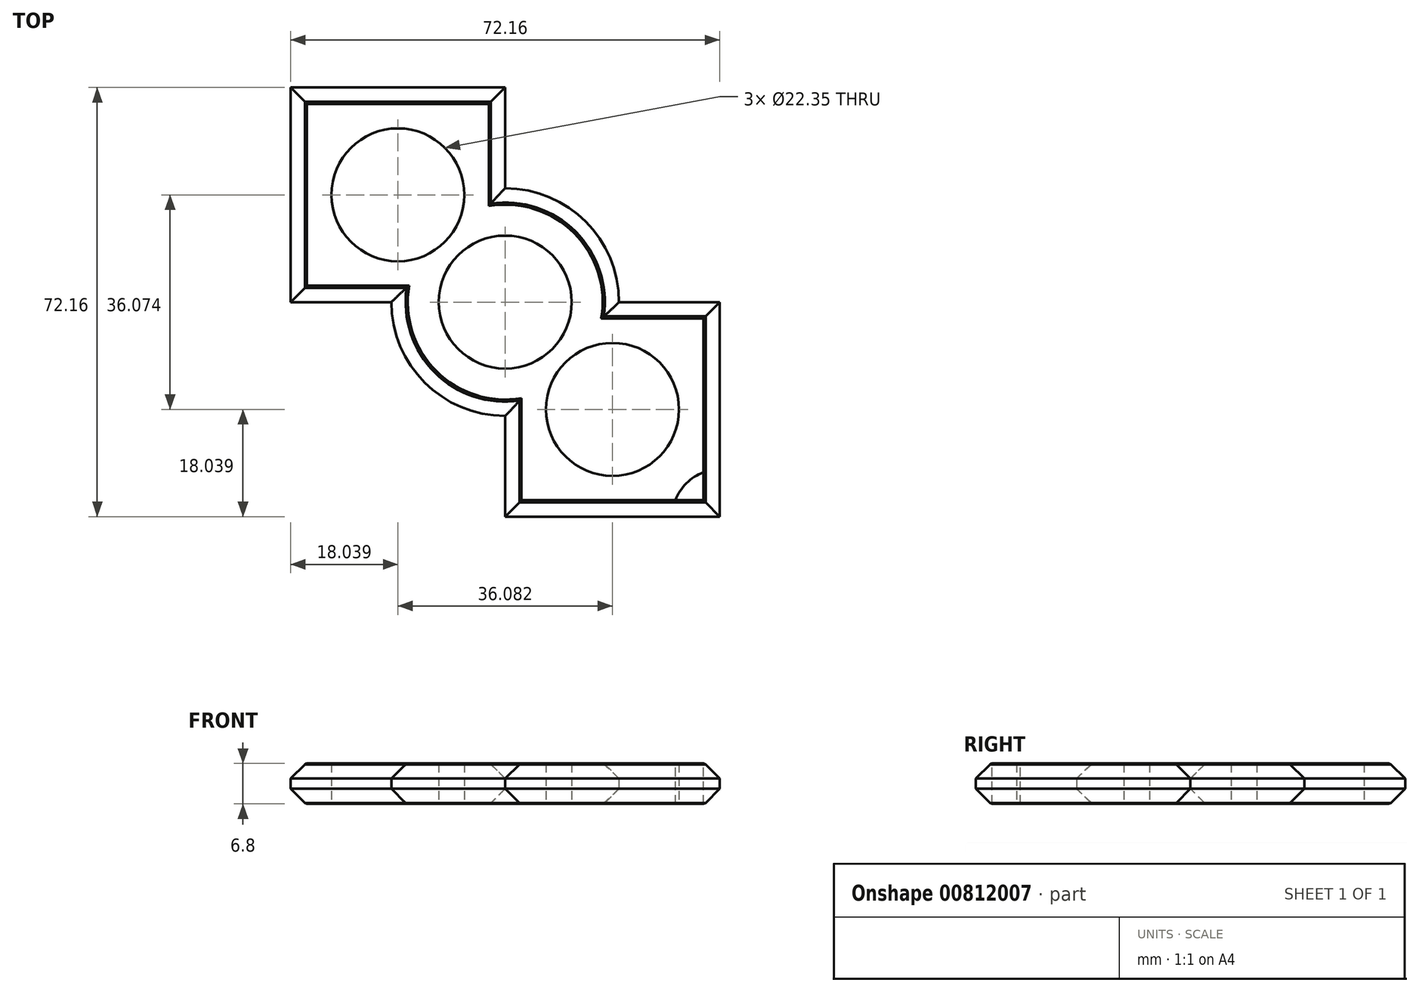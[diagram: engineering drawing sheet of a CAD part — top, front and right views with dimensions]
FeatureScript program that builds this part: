
annotation { "Feature Type Name" : "Feature", "Feature Type Description" : "" }
export const myFeature = defineFeature(function(context is Context, id is Id, definition is map)
    precondition{}
    {
        {
            var Q0;
            Q0=qCreatedBy(makeId("Top.planeOp"),FACE);
            var sketch = newSketch(context, id + "F0", { "sketchPlane" : qUnion([Q0])});
            skLineSegment(sketch, "E0.bottom", {"start": v(0, 0) * mm, "end": v(-36.08, 0) * mm});
            skLineSegment(sketch, "E0.top", {"start": v(0, 36.08) * mm, "end": v(-36.08, 36.08) * mm});
            skLineSegment(sketch, "E0.left", {"start": v(0, 0) * mm, "end": v(0, 36.08) * mm});
            skLineSegment(sketch, "E0.right", {"start": v(-36.08, 0) * mm, "end": v(-36.08, 36.08) * mm});
            skLineSegment(sketch, "E1.bottom", {"start": v(0, 0) * mm, "end": v(36.08, 0) * mm});
            skLineSegment(sketch, "E1.top", {"start": v(0, -36.08) * mm, "end": v(36.08, -36.08) * mm});
            skLineSegment(sketch, "E1.left", {"start": v(0, 0) * mm, "end": v(0, -36.08) * mm});
            skLineSegment(sketch, "E1.right", {"start": v(36.08, 0) * mm, "end": v(36.08, -36.08) * mm});
            skCircle(sketch, "E2", {"center": v(0, 0) * mm, "radius": 19.14 * mm});
            skCircle(sketch, "E3", {"center": v(18.04, -18.04) * mm, "radius": 11.18 * mm});
            skCircle(sketch, "E4", {"center": v(0, 0) * mm, "radius": 11.18 * mm});
            skCircle(sketch, "E5", {"center": v(-18.04, 18.03) * mm, "radius": 11.18 * mm});
            skLineSegment(sketch, "E6", {"start": v(-36.08, 36.08) * mm, "end": v(36.08, -36.08) * mm});
            skLineSegment(sketch, "E7", {"start": v(0, 36.08) * mm, "end": v(-36.08, 0) * mm});
            skLineSegment(sketch, "E8", {"start": v(36.08, 0) * mm, "end": v(0, -36.08) * mm});
            skPoint(sketch, "E9.positionSnap0", {"position": v(-18.04, 18.04) * mm});
            skSolve(sketch);
        }
        {
            var Q0;
            Q0 = qSketchRegion(id + "F0", true);
            extrude(context, id + "F1", {"entities" : qUnion([Q0]), "depth" : 6.8 * mm, "offsetDistance" : 25.4 * mm});
        }
        {
            var Q0;
            {var subQ0=sQuery(id+"F0.wireOp",EDGE,"E2");Q0=makeQuery(id+"F1.opExtrude","CAP_EDGE",EDGE,{"disambiguationData":[OSD([subQ0]),TDD([makeQuery(id+"F0.imprint","IMPRINT",EDGE,{"disambiguationData":[TD([[makeQuery(id+"F0.imprint","INTERSECT",VERTEX,{"derivedFrom":[sQuery(id+"F0.wireOp",EDGE,"E0.bottom"),subQ0]}),-1.0]])],"derivedFrom":subQ0})])],"isStart":false});}
            var Q1;
            {var subQ0=sQuery(id+"F0.wireOp",EDGE,"E2");Q1=makeQuery(id+"F1.opExtrude","CAP_EDGE",EDGE,{"disambiguationData":[OSD([subQ0]),TDD([makeQuery(id+"F0.imprint","IMPRINT",EDGE,{"disambiguationData":[TD([[makeQuery(id+"F0.imprint","INTERSECT",VERTEX,{"derivedFrom":[sQuery(id+"F0.wireOp",EDGE,"E0.bottom"),subQ0]}),-1.0]])],"derivedFrom":subQ0})])],"isStart":true});}
            var Q2;
            Q2=makeQuery(id+"F1.opExtrude","CAP_EDGE",EDGE,{"disambiguationData":[OSD([sQuery(id+"F0.wireOp",EDGE,"E0.bottom")])],"isStart":false});
            var Q3;
            Q3=makeQuery(id+"F1.opExtrude","CAP_EDGE",EDGE,{"disambiguationData":[OSD([sQuery(id+"F0.wireOp",EDGE,"E0.bottom")])],"isStart":true});
            var Q4;
            Q4=makeQuery(id+"F1.opExtrude","CAP_EDGE",EDGE,{"disambiguationData":[OSD([sQuery(id+"F0.wireOp",EDGE,"E1.top")])],"isStart":false});
            var Q5;
            Q5=makeQuery(id+"F1.opExtrude","CAP_EDGE",EDGE,{"disambiguationData":[OSD([sQuery(id+"F0.wireOp",EDGE,"E1.top")])],"isStart":true});
            var Q6;
            Q6=makeQuery(id+"F1.opExtrude","CAP_EDGE",EDGE,{"disambiguationData":[OSD([sQuery(id+"F0.wireOp",EDGE,"E1.left")])],"isStart":true});
            var Q7;
            Q7=makeQuery(id+"F1.opExtrude","CAP_EDGE",EDGE,{"disambiguationData":[OSD([sQuery(id+"F0.wireOp",EDGE,"E1.left")])],"isStart":false});
            var Q8;
            Q8=makeQuery(id+"F1.opExtrude","CAP_EDGE",EDGE,{"disambiguationData":[OSD([sQuery(id+"F0.wireOp",EDGE,"E1.right")])],"isStart":false});
            var Q9;
            Q9=makeQuery(id+"F1.opExtrude","CAP_EDGE",EDGE,{"disambiguationData":[OSD([sQuery(id+"F0.wireOp",EDGE,"E1.right")])],"isStart":true});
            var Q10;
            Q10=makeQuery(id+"F1.opExtrude","CAP_EDGE",EDGE,{"disambiguationData":[OSD([sQuery(id+"F0.wireOp",EDGE,"E1.bottom")])],"isStart":true});
            var Q11;
            Q11=makeQuery(id+"F1.opExtrude","CAP_EDGE",EDGE,{"disambiguationData":[OSD([sQuery(id+"F0.wireOp",EDGE,"E1.bottom")])],"isStart":false});
            var Q12;
            {var subQ0=sQuery(id+"F0.wireOp",EDGE,"E2");Q12=makeQuery(id+"F1.opExtrude","CAP_EDGE",EDGE,{"disambiguationData":[OSD([subQ0]),TDD([makeQuery(id+"F0.imprint","IMPRINT",EDGE,{"disambiguationData":[TD([[makeQuery(id+"F0.imprint","INTERSECT",VERTEX,{"derivedFrom":[sQuery(id+"F0.wireOp",EDGE,"E0.left"),subQ0]}),1.0]])],"derivedFrom":subQ0})])],"isStart":false});}
            var Q13;
            {var subQ0=sQuery(id+"F0.wireOp",EDGE,"E2");Q13=makeQuery(id+"F1.opExtrude","CAP_EDGE",EDGE,{"disambiguationData":[OSD([subQ0]),TDD([makeQuery(id+"F0.imprint","IMPRINT",EDGE,{"disambiguationData":[TD([[makeQuery(id+"F0.imprint","INTERSECT",VERTEX,{"derivedFrom":[sQuery(id+"F0.wireOp",EDGE,"E0.left"),subQ0]}),1.0]])],"derivedFrom":subQ0})])],"isStart":true});}
            var Q14;
            Q14=makeQuery(id+"F1.opExtrude","CAP_EDGE",EDGE,{"disambiguationData":[OSD([sQuery(id+"F0.wireOp",EDGE,"E0.left")])],"isStart":false});
            var Q15;
            Q15=makeQuery(id+"F1.opExtrude","CAP_EDGE",EDGE,{"disambiguationData":[OSD([sQuery(id+"F0.wireOp",EDGE,"E0.left")])],"isStart":true});
            var Q16;
            Q16=makeQuery(id+"F1.opExtrude","CAP_EDGE",EDGE,{"disambiguationData":[OSD([sQuery(id+"F0.wireOp",EDGE,"E0.top")])],"isStart":true});
            var Q17;
            Q17=makeQuery(id+"F1.opExtrude","CAP_EDGE",EDGE,{"disambiguationData":[OSD([sQuery(id+"F0.wireOp",EDGE,"E0.top")])],"isStart":false});
            var Q18;
            Q18=makeQuery(id+"F1.opExtrude","CAP_EDGE",EDGE,{"disambiguationData":[OSD([sQuery(id+"F0.wireOp",EDGE,"E0.right")])],"isStart":false});
            var Q19;
            Q19=makeQuery(id+"F1.opExtrude","CAP_EDGE",EDGE,{"disambiguationData":[OSD([sQuery(id+"F0.wireOp",EDGE,"E0.right")])],"isStart":true});
            chamfer(context, id + "F2", {"entities" : qUnion([Q0, Q1, Q2, Q3, Q4, Q5, Q6, Q7, Q8, Q9, Q10, Q11, Q12, Q13, Q14, Q15, Q16, Q17, Q18, Q19]), "width" : 2.54 * mm, "tangentPropagation" : true});
        }
        {
            var Q0;
            {var subQ0=sQuery(id+"F0.wireOp",EDGE,"E0.right");Q0=makeQuery(id+"F2.opChamfer","BLEND_EDGE",EDGE,{"blendedFrom":[makeQuery(id+"F1.opExtrude","CAP_EDGE",EDGE,{"disambiguationData":[OSD([subQ0])],"isStart":false}),makeQuery(id+"F1.opExtrude","CAP_FACE",FACE,{"disambiguationData":[OSD([sQuery(id+"F0.wireOp",EDGE,"E0.bottom"),sQuery(id+"F0.wireOp",EDGE,"E0.top"),sQuery(id+"F0.wireOp",EDGE,"E0.left"),subQ0,sQuery(id+"F0.wireOp",EDGE,"E1.bottom"),sQuery(id+"F0.wireOp",EDGE,"E1.top"),sQuery(id+"F0.wireOp",EDGE,"E1.left"),sQuery(id+"F0.wireOp",EDGE,"E1.right"),sQuery(id+"F0.wireOp",EDGE,"E2"),sQuery(id+"F0.wireOp",EDGE,"VLRDwp0t-7qAt-eu2T-jZEU-YPBGhESBlTfT"),sQuery(id+"F0.wireOp",EDGE,"WEYKgsFz-RtNv-legM-eSOE-KK9nOp16vvV1"),sQuery(id+"F0.wireOp",EDGE,"XJheyNme-LiQL-8ZLm-PUsm-MQK8YgGBS3Id")])],"isStart":false})],"blendedInto":[makeQuery(id+"F1.opExtrude","CAP_FACE",FACE,{"disambiguationData":[OSD([sQuery(id+"F0.wireOp",EDGE,"E0.bottom"),sQuery(id+"F0.wireOp",EDGE,"E0.top"),sQuery(id+"F0.wireOp",EDGE,"E0.left"),subQ0,sQuery(id+"F0.wireOp",EDGE,"E1.bottom"),sQuery(id+"F0.wireOp",EDGE,"E1.top"),sQuery(id+"F0.wireOp",EDGE,"E1.left"),sQuery(id+"F0.wireOp",EDGE,"E1.right"),sQuery(id+"F0.wireOp",EDGE,"E2"),sQuery(id+"F0.wireOp",EDGE,"VLRDwp0t-7qAt-eu2T-jZEU-YPBGhESBlTfT"),sQuery(id+"F0.wireOp",EDGE,"WEYKgsFz-RtNv-legM-eSOE-KK9nOp16vvV1"),sQuery(id+"F0.wireOp",EDGE,"XJheyNme-LiQL-8ZLm-PUsm-MQK8YgGBS3Id")])],"isStart":false})]});}
            var Q1;
            {var subQ0=sQuery(id+"F0.wireOp",EDGE,"E0.bottom");Q1=makeQuery(id+"F2.opChamfer","BLEND_EDGE",EDGE,{"blendedFrom":[makeQuery(id+"F1.opExtrude","CAP_EDGE",EDGE,{"disambiguationData":[OSD([subQ0])],"isStart":false}),makeQuery(id+"F1.opExtrude","CAP_FACE",FACE,{"disambiguationData":[OSD([subQ0,sQuery(id+"F0.wireOp",EDGE,"E0.top"),sQuery(id+"F0.wireOp",EDGE,"E0.left"),sQuery(id+"F0.wireOp",EDGE,"E0.right"),sQuery(id+"F0.wireOp",EDGE,"E1.bottom"),sQuery(id+"F0.wireOp",EDGE,"E1.top"),sQuery(id+"F0.wireOp",EDGE,"E1.left"),sQuery(id+"F0.wireOp",EDGE,"E1.right"),sQuery(id+"F0.wireOp",EDGE,"E2"),sQuery(id+"F0.wireOp",EDGE,"VLRDwp0t-7qAt-eu2T-jZEU-YPBGhESBlTfT"),sQuery(id+"F0.wireOp",EDGE,"WEYKgsFz-RtNv-legM-eSOE-KK9nOp16vvV1"),sQuery(id+"F0.wireOp",EDGE,"XJheyNme-LiQL-8ZLm-PUsm-MQK8YgGBS3Id")])],"isStart":false})],"blendedInto":[makeQuery(id+"F1.opExtrude","CAP_FACE",FACE,{"disambiguationData":[OSD([subQ0,sQuery(id+"F0.wireOp",EDGE,"E0.top"),sQuery(id+"F0.wireOp",EDGE,"E0.left"),sQuery(id+"F0.wireOp",EDGE,"E0.right"),sQuery(id+"F0.wireOp",EDGE,"E1.bottom"),sQuery(id+"F0.wireOp",EDGE,"E1.top"),sQuery(id+"F0.wireOp",EDGE,"E1.left"),sQuery(id+"F0.wireOp",EDGE,"E1.right"),sQuery(id+"F0.wireOp",EDGE,"E2"),sQuery(id+"F0.wireOp",EDGE,"VLRDwp0t-7qAt-eu2T-jZEU-YPBGhESBlTfT"),sQuery(id+"F0.wireOp",EDGE,"WEYKgsFz-RtNv-legM-eSOE-KK9nOp16vvV1"),sQuery(id+"F0.wireOp",EDGE,"XJheyNme-LiQL-8ZLm-PUsm-MQK8YgGBS3Id")])],"isStart":false})]});}
            var Q2;
            {var subQ0=sQuery(id+"F0.wireOp",EDGE,"E2");var subQ1=sQuery(id+"F0.wireOp",EDGE,"E1.left");var subQ2=sQuery(id+"F0.wireOp",EDGE,"E0.bottom");Q2=makeQuery(id+"F2.opChamfer","BLEND_EDGE",EDGE,{"blendedFrom":[makeQuery(id+"F1.opExtrude","CAP_EDGE",EDGE,{"disambiguationData":[OSD([subQ0]),TDD([makeQuery(id+"F0.imprint","IMPRINT",EDGE,{"disambiguationData":[TD([[makeQuery(id+"F0.imprint","INTERSECT",VERTEX,{"derivedFrom":[subQ2,subQ0]}),-1.0]])],"derivedFrom":subQ0})])],"isStart":false}),makeQuery(id+"F1.opExtrude","CAP_FACE",FACE,{"disambiguationData":[OSD([subQ2,sQuery(id+"F0.wireOp",EDGE,"E0.top"),sQuery(id+"F0.wireOp",EDGE,"E0.left"),sQuery(id+"F0.wireOp",EDGE,"E0.right"),sQuery(id+"F0.wireOp",EDGE,"E1.bottom"),sQuery(id+"F0.wireOp",EDGE,"E1.top"),subQ1,sQuery(id+"F0.wireOp",EDGE,"E1.right"),subQ0,sQuery(id+"F0.wireOp",EDGE,"VLRDwp0t-7qAt-eu2T-jZEU-YPBGhESBlTfT"),sQuery(id+"F0.wireOp",EDGE,"WEYKgsFz-RtNv-legM-eSOE-KK9nOp16vvV1"),sQuery(id+"F0.wireOp",EDGE,"XJheyNme-LiQL-8ZLm-PUsm-MQK8YgGBS3Id")])],"isStart":false})],"blendedInto":[makeQuery(id+"F1.opExtrude","CAP_FACE",FACE,{"disambiguationData":[OSD([subQ2,sQuery(id+"F0.wireOp",EDGE,"E0.top"),sQuery(id+"F0.wireOp",EDGE,"E0.left"),sQuery(id+"F0.wireOp",EDGE,"E0.right"),sQuery(id+"F0.wireOp",EDGE,"E1.bottom"),sQuery(id+"F0.wireOp",EDGE,"E1.top"),subQ1,sQuery(id+"F0.wireOp",EDGE,"E1.right"),subQ0,sQuery(id+"F0.wireOp",EDGE,"VLRDwp0t-7qAt-eu2T-jZEU-YPBGhESBlTfT"),sQuery(id+"F0.wireOp",EDGE,"WEYKgsFz-RtNv-legM-eSOE-KK9nOp16vvV1"),sQuery(id+"F0.wireOp",EDGE,"XJheyNme-LiQL-8ZLm-PUsm-MQK8YgGBS3Id")])],"isStart":false})]});}
            var Q3;
            {var subQ0=sQuery(id+"F0.wireOp",EDGE,"E1.left");Q3=makeQuery(id+"F2.opChamfer","BLEND_EDGE",EDGE,{"blendedFrom":[makeQuery(id+"F1.opExtrude","CAP_EDGE",EDGE,{"disambiguationData":[OSD([subQ0])],"isStart":false}),makeQuery(id+"F1.opExtrude","CAP_FACE",FACE,{"disambiguationData":[OSD([sQuery(id+"F0.wireOp",EDGE,"E0.bottom"),sQuery(id+"F0.wireOp",EDGE,"E0.top"),sQuery(id+"F0.wireOp",EDGE,"E0.left"),sQuery(id+"F0.wireOp",EDGE,"E0.right"),sQuery(id+"F0.wireOp",EDGE,"E1.bottom"),sQuery(id+"F0.wireOp",EDGE,"E1.top"),subQ0,sQuery(id+"F0.wireOp",EDGE,"E1.right"),sQuery(id+"F0.wireOp",EDGE,"E2"),sQuery(id+"F0.wireOp",EDGE,"VLRDwp0t-7qAt-eu2T-jZEU-YPBGhESBlTfT"),sQuery(id+"F0.wireOp",EDGE,"WEYKgsFz-RtNv-legM-eSOE-KK9nOp16vvV1"),sQuery(id+"F0.wireOp",EDGE,"XJheyNme-LiQL-8ZLm-PUsm-MQK8YgGBS3Id")])],"isStart":false})],"blendedInto":[makeQuery(id+"F1.opExtrude","CAP_FACE",FACE,{"disambiguationData":[OSD([sQuery(id+"F0.wireOp",EDGE,"E0.bottom"),sQuery(id+"F0.wireOp",EDGE,"E0.top"),sQuery(id+"F0.wireOp",EDGE,"E0.left"),sQuery(id+"F0.wireOp",EDGE,"E0.right"),sQuery(id+"F0.wireOp",EDGE,"E1.bottom"),sQuery(id+"F0.wireOp",EDGE,"E1.top"),subQ0,sQuery(id+"F0.wireOp",EDGE,"E1.right"),sQuery(id+"F0.wireOp",EDGE,"E2"),sQuery(id+"F0.wireOp",EDGE,"VLRDwp0t-7qAt-eu2T-jZEU-YPBGhESBlTfT"),sQuery(id+"F0.wireOp",EDGE,"WEYKgsFz-RtNv-legM-eSOE-KK9nOp16vvV1"),sQuery(id+"F0.wireOp",EDGE,"XJheyNme-LiQL-8ZLm-PUsm-MQK8YgGBS3Id")])],"isStart":false})]});}
            var Q4;
            {var subQ0=sQuery(id+"F0.wireOp",EDGE,"E1.top");Q4=makeQuery(id+"F2.opChamfer","BLEND_EDGE",EDGE,{"blendedFrom":[makeQuery(id+"F1.opExtrude","CAP_EDGE",EDGE,{"disambiguationData":[OSD([subQ0])],"isStart":false}),makeQuery(id+"F1.opExtrude","CAP_FACE",FACE,{"disambiguationData":[OSD([sQuery(id+"F0.wireOp",EDGE,"E0.bottom"),sQuery(id+"F0.wireOp",EDGE,"E0.top"),sQuery(id+"F0.wireOp",EDGE,"E0.left"),sQuery(id+"F0.wireOp",EDGE,"E0.right"),sQuery(id+"F0.wireOp",EDGE,"E1.bottom"),subQ0,sQuery(id+"F0.wireOp",EDGE,"E1.left"),sQuery(id+"F0.wireOp",EDGE,"E1.right"),sQuery(id+"F0.wireOp",EDGE,"E2"),sQuery(id+"F0.wireOp",EDGE,"VLRDwp0t-7qAt-eu2T-jZEU-YPBGhESBlTfT"),sQuery(id+"F0.wireOp",EDGE,"WEYKgsFz-RtNv-legM-eSOE-KK9nOp16vvV1"),sQuery(id+"F0.wireOp",EDGE,"XJheyNme-LiQL-8ZLm-PUsm-MQK8YgGBS3Id")])],"isStart":false})],"blendedInto":[makeQuery(id+"F1.opExtrude","CAP_FACE",FACE,{"disambiguationData":[OSD([sQuery(id+"F0.wireOp",EDGE,"E0.bottom"),sQuery(id+"F0.wireOp",EDGE,"E0.top"),sQuery(id+"F0.wireOp",EDGE,"E0.left"),sQuery(id+"F0.wireOp",EDGE,"E0.right"),sQuery(id+"F0.wireOp",EDGE,"E1.bottom"),subQ0,sQuery(id+"F0.wireOp",EDGE,"E1.left"),sQuery(id+"F0.wireOp",EDGE,"E1.right"),sQuery(id+"F0.wireOp",EDGE,"E2"),sQuery(id+"F0.wireOp",EDGE,"VLRDwp0t-7qAt-eu2T-jZEU-YPBGhESBlTfT"),sQuery(id+"F0.wireOp",EDGE,"WEYKgsFz-RtNv-legM-eSOE-KK9nOp16vvV1"),sQuery(id+"F0.wireOp",EDGE,"XJheyNme-LiQL-8ZLm-PUsm-MQK8YgGBS3Id")])],"isStart":false})]});}
            var Q5;
            {var subQ0=sQuery(id+"F0.wireOp",EDGE,"E1.right");Q5=makeQuery(id+"F2.opChamfer","BLEND_EDGE",EDGE,{"blendedFrom":[makeQuery(id+"F1.opExtrude","CAP_EDGE",EDGE,{"disambiguationData":[OSD([subQ0])],"isStart":false}),makeQuery(id+"F1.opExtrude","CAP_FACE",FACE,{"disambiguationData":[OSD([sQuery(id+"F0.wireOp",EDGE,"E0.bottom"),sQuery(id+"F0.wireOp",EDGE,"E0.top"),sQuery(id+"F0.wireOp",EDGE,"E0.left"),sQuery(id+"F0.wireOp",EDGE,"E0.right"),sQuery(id+"F0.wireOp",EDGE,"E1.bottom"),sQuery(id+"F0.wireOp",EDGE,"E1.top"),sQuery(id+"F0.wireOp",EDGE,"E1.left"),subQ0,sQuery(id+"F0.wireOp",EDGE,"E2"),sQuery(id+"F0.wireOp",EDGE,"VLRDwp0t-7qAt-eu2T-jZEU-YPBGhESBlTfT"),sQuery(id+"F0.wireOp",EDGE,"WEYKgsFz-RtNv-legM-eSOE-KK9nOp16vvV1"),sQuery(id+"F0.wireOp",EDGE,"XJheyNme-LiQL-8ZLm-PUsm-MQK8YgGBS3Id")])],"isStart":false})],"blendedInto":[makeQuery(id+"F1.opExtrude","CAP_FACE",FACE,{"disambiguationData":[OSD([sQuery(id+"F0.wireOp",EDGE,"E0.bottom"),sQuery(id+"F0.wireOp",EDGE,"E0.top"),sQuery(id+"F0.wireOp",EDGE,"E0.left"),sQuery(id+"F0.wireOp",EDGE,"E0.right"),sQuery(id+"F0.wireOp",EDGE,"E1.bottom"),sQuery(id+"F0.wireOp",EDGE,"E1.top"),sQuery(id+"F0.wireOp",EDGE,"E1.left"),subQ0,sQuery(id+"F0.wireOp",EDGE,"E2"),sQuery(id+"F0.wireOp",EDGE,"VLRDwp0t-7qAt-eu2T-jZEU-YPBGhESBlTfT"),sQuery(id+"F0.wireOp",EDGE,"WEYKgsFz-RtNv-legM-eSOE-KK9nOp16vvV1"),sQuery(id+"F0.wireOp",EDGE,"XJheyNme-LiQL-8ZLm-PUsm-MQK8YgGBS3Id")])],"isStart":false})]});}
            var Q6;
            {var subQ0=sQuery(id+"F0.wireOp",EDGE,"E1.bottom");Q6=makeQuery(id+"F2.opChamfer","BLEND_EDGE",EDGE,{"blendedFrom":[makeQuery(id+"F1.opExtrude","CAP_EDGE",EDGE,{"disambiguationData":[OSD([subQ0])],"isStart":false}),makeQuery(id+"F1.opExtrude","CAP_FACE",FACE,{"disambiguationData":[OSD([sQuery(id+"F0.wireOp",EDGE,"E0.bottom"),sQuery(id+"F0.wireOp",EDGE,"E0.top"),sQuery(id+"F0.wireOp",EDGE,"E0.left"),sQuery(id+"F0.wireOp",EDGE,"E0.right"),subQ0,sQuery(id+"F0.wireOp",EDGE,"E1.top"),sQuery(id+"F0.wireOp",EDGE,"E1.left"),sQuery(id+"F0.wireOp",EDGE,"E1.right"),sQuery(id+"F0.wireOp",EDGE,"E2"),sQuery(id+"F0.wireOp",EDGE,"VLRDwp0t-7qAt-eu2T-jZEU-YPBGhESBlTfT"),sQuery(id+"F0.wireOp",EDGE,"WEYKgsFz-RtNv-legM-eSOE-KK9nOp16vvV1"),sQuery(id+"F0.wireOp",EDGE,"XJheyNme-LiQL-8ZLm-PUsm-MQK8YgGBS3Id")])],"isStart":false})],"blendedInto":[makeQuery(id+"F1.opExtrude","CAP_FACE",FACE,{"disambiguationData":[OSD([sQuery(id+"F0.wireOp",EDGE,"E0.bottom"),sQuery(id+"F0.wireOp",EDGE,"E0.top"),sQuery(id+"F0.wireOp",EDGE,"E0.left"),sQuery(id+"F0.wireOp",EDGE,"E0.right"),subQ0,sQuery(id+"F0.wireOp",EDGE,"E1.top"),sQuery(id+"F0.wireOp",EDGE,"E1.left"),sQuery(id+"F0.wireOp",EDGE,"E1.right"),sQuery(id+"F0.wireOp",EDGE,"E2"),sQuery(id+"F0.wireOp",EDGE,"VLRDwp0t-7qAt-eu2T-jZEU-YPBGhESBlTfT"),sQuery(id+"F0.wireOp",EDGE,"WEYKgsFz-RtNv-legM-eSOE-KK9nOp16vvV1"),sQuery(id+"F0.wireOp",EDGE,"XJheyNme-LiQL-8ZLm-PUsm-MQK8YgGBS3Id")])],"isStart":false})]});}
            var Q7;
            {var subQ0=sQuery(id+"F0.wireOp",EDGE,"E2");var subQ1=sQuery(id+"F0.wireOp",EDGE,"E1.bottom");var subQ2=sQuery(id+"F0.wireOp",EDGE,"E0.left");Q7=makeQuery(id+"F2.opChamfer","BLEND_EDGE",EDGE,{"blendedFrom":[makeQuery(id+"F1.opExtrude","CAP_EDGE",EDGE,{"disambiguationData":[OSD([subQ0]),TDD([makeQuery(id+"F0.imprint","IMPRINT",EDGE,{"disambiguationData":[TD([[makeQuery(id+"F0.imprint","INTERSECT",VERTEX,{"derivedFrom":[subQ2,subQ0]}),1.0]])],"derivedFrom":subQ0})])],"isStart":false}),makeQuery(id+"F1.opExtrude","CAP_FACE",FACE,{"disambiguationData":[OSD([sQuery(id+"F0.wireOp",EDGE,"E0.bottom"),sQuery(id+"F0.wireOp",EDGE,"E0.top"),subQ2,sQuery(id+"F0.wireOp",EDGE,"E0.right"),subQ1,sQuery(id+"F0.wireOp",EDGE,"E1.top"),sQuery(id+"F0.wireOp",EDGE,"E1.left"),sQuery(id+"F0.wireOp",EDGE,"E1.right"),subQ0,sQuery(id+"F0.wireOp",EDGE,"VLRDwp0t-7qAt-eu2T-jZEU-YPBGhESBlTfT"),sQuery(id+"F0.wireOp",EDGE,"WEYKgsFz-RtNv-legM-eSOE-KK9nOp16vvV1"),sQuery(id+"F0.wireOp",EDGE,"XJheyNme-LiQL-8ZLm-PUsm-MQK8YgGBS3Id")])],"isStart":false})],"blendedInto":[makeQuery(id+"F1.opExtrude","CAP_FACE",FACE,{"disambiguationData":[OSD([sQuery(id+"F0.wireOp",EDGE,"E0.bottom"),sQuery(id+"F0.wireOp",EDGE,"E0.top"),subQ2,sQuery(id+"F0.wireOp",EDGE,"E0.right"),subQ1,sQuery(id+"F0.wireOp",EDGE,"E1.top"),sQuery(id+"F0.wireOp",EDGE,"E1.left"),sQuery(id+"F0.wireOp",EDGE,"E1.right"),subQ0,sQuery(id+"F0.wireOp",EDGE,"VLRDwp0t-7qAt-eu2T-jZEU-YPBGhESBlTfT"),sQuery(id+"F0.wireOp",EDGE,"WEYKgsFz-RtNv-legM-eSOE-KK9nOp16vvV1"),sQuery(id+"F0.wireOp",EDGE,"XJheyNme-LiQL-8ZLm-PUsm-MQK8YgGBS3Id")])],"isStart":false})]});}
            var Q8;
            {var subQ0=sQuery(id+"F0.wireOp",EDGE,"E0.left");Q8=makeQuery(id+"F2.opChamfer","BLEND_EDGE",EDGE,{"blendedFrom":[makeQuery(id+"F1.opExtrude","CAP_EDGE",EDGE,{"disambiguationData":[OSD([subQ0])],"isStart":false}),makeQuery(id+"F1.opExtrude","CAP_FACE",FACE,{"disambiguationData":[OSD([sQuery(id+"F0.wireOp",EDGE,"E0.bottom"),sQuery(id+"F0.wireOp",EDGE,"E0.top"),subQ0,sQuery(id+"F0.wireOp",EDGE,"E0.right"),sQuery(id+"F0.wireOp",EDGE,"E1.bottom"),sQuery(id+"F0.wireOp",EDGE,"E1.top"),sQuery(id+"F0.wireOp",EDGE,"E1.left"),sQuery(id+"F0.wireOp",EDGE,"E1.right"),sQuery(id+"F0.wireOp",EDGE,"E2"),sQuery(id+"F0.wireOp",EDGE,"VLRDwp0t-7qAt-eu2T-jZEU-YPBGhESBlTfT"),sQuery(id+"F0.wireOp",EDGE,"WEYKgsFz-RtNv-legM-eSOE-KK9nOp16vvV1"),sQuery(id+"F0.wireOp",EDGE,"XJheyNme-LiQL-8ZLm-PUsm-MQK8YgGBS3Id")])],"isStart":false})],"blendedInto":[makeQuery(id+"F1.opExtrude","CAP_FACE",FACE,{"disambiguationData":[OSD([sQuery(id+"F0.wireOp",EDGE,"E0.bottom"),sQuery(id+"F0.wireOp",EDGE,"E0.top"),subQ0,sQuery(id+"F0.wireOp",EDGE,"E0.right"),sQuery(id+"F0.wireOp",EDGE,"E1.bottom"),sQuery(id+"F0.wireOp",EDGE,"E1.top"),sQuery(id+"F0.wireOp",EDGE,"E1.left"),sQuery(id+"F0.wireOp",EDGE,"E1.right"),sQuery(id+"F0.wireOp",EDGE,"E2"),sQuery(id+"F0.wireOp",EDGE,"VLRDwp0t-7qAt-eu2T-jZEU-YPBGhESBlTfT"),sQuery(id+"F0.wireOp",EDGE,"WEYKgsFz-RtNv-legM-eSOE-KK9nOp16vvV1"),sQuery(id+"F0.wireOp",EDGE,"XJheyNme-LiQL-8ZLm-PUsm-MQK8YgGBS3Id")])],"isStart":false})]});}
            var Q9;
            {var subQ0=sQuery(id+"F0.wireOp",EDGE,"E0.top");Q9=makeQuery(id+"F2.opChamfer","BLEND_EDGE",EDGE,{"blendedFrom":[makeQuery(id+"F1.opExtrude","CAP_EDGE",EDGE,{"disambiguationData":[OSD([subQ0])],"isStart":false}),makeQuery(id+"F1.opExtrude","CAP_FACE",FACE,{"disambiguationData":[OSD([sQuery(id+"F0.wireOp",EDGE,"E0.bottom"),subQ0,sQuery(id+"F0.wireOp",EDGE,"E0.left"),sQuery(id+"F0.wireOp",EDGE,"E0.right"),sQuery(id+"F0.wireOp",EDGE,"E1.bottom"),sQuery(id+"F0.wireOp",EDGE,"E1.top"),sQuery(id+"F0.wireOp",EDGE,"E1.left"),sQuery(id+"F0.wireOp",EDGE,"E1.right"),sQuery(id+"F0.wireOp",EDGE,"E2"),sQuery(id+"F0.wireOp",EDGE,"VLRDwp0t-7qAt-eu2T-jZEU-YPBGhESBlTfT"),sQuery(id+"F0.wireOp",EDGE,"WEYKgsFz-RtNv-legM-eSOE-KK9nOp16vvV1"),sQuery(id+"F0.wireOp",EDGE,"XJheyNme-LiQL-8ZLm-PUsm-MQK8YgGBS3Id")])],"isStart":false})],"blendedInto":[makeQuery(id+"F1.opExtrude","CAP_FACE",FACE,{"disambiguationData":[OSD([sQuery(id+"F0.wireOp",EDGE,"E0.bottom"),subQ0,sQuery(id+"F0.wireOp",EDGE,"E0.left"),sQuery(id+"F0.wireOp",EDGE,"E0.right"),sQuery(id+"F0.wireOp",EDGE,"E1.bottom"),sQuery(id+"F0.wireOp",EDGE,"E1.top"),sQuery(id+"F0.wireOp",EDGE,"E1.left"),sQuery(id+"F0.wireOp",EDGE,"E1.right"),sQuery(id+"F0.wireOp",EDGE,"E2"),sQuery(id+"F0.wireOp",EDGE,"VLRDwp0t-7qAt-eu2T-jZEU-YPBGhESBlTfT"),sQuery(id+"F0.wireOp",EDGE,"WEYKgsFz-RtNv-legM-eSOE-KK9nOp16vvV1"),sQuery(id+"F0.wireOp",EDGE,"XJheyNme-LiQL-8ZLm-PUsm-MQK8YgGBS3Id")])],"isStart":false})]});}
            var Q10;
            {var subQ0=sQuery(id+"F0.wireOp",EDGE,"E1.right");Q10=makeQuery(id+"F2.opChamfer","BLEND_EDGE",EDGE,{"blendedFrom":[makeQuery(id+"F1.opExtrude","CAP_EDGE",EDGE,{"disambiguationData":[OSD([subQ0])],"isStart":true}),makeQuery(id+"F1.opExtrude","CAP_FACE",FACE,{"disambiguationData":[OSD([sQuery(id+"F0.wireOp",EDGE,"E0.bottom"),sQuery(id+"F0.wireOp",EDGE,"E0.top"),sQuery(id+"F0.wireOp",EDGE,"E0.left"),sQuery(id+"F0.wireOp",EDGE,"E0.right"),sQuery(id+"F0.wireOp",EDGE,"E1.bottom"),sQuery(id+"F0.wireOp",EDGE,"E1.top"),sQuery(id+"F0.wireOp",EDGE,"E1.left"),subQ0,sQuery(id+"F0.wireOp",EDGE,"E2"),sQuery(id+"F0.wireOp",EDGE,"VLRDwp0t-7qAt-eu2T-jZEU-YPBGhESBlTfT"),sQuery(id+"F0.wireOp",EDGE,"WEYKgsFz-RtNv-legM-eSOE-KK9nOp16vvV1"),sQuery(id+"F0.wireOp",EDGE,"XJheyNme-LiQL-8ZLm-PUsm-MQK8YgGBS3Id")])],"isStart":true})],"blendedInto":[makeQuery(id+"F1.opExtrude","CAP_FACE",FACE,{"disambiguationData":[OSD([sQuery(id+"F0.wireOp",EDGE,"E0.bottom"),sQuery(id+"F0.wireOp",EDGE,"E0.top"),sQuery(id+"F0.wireOp",EDGE,"E0.left"),sQuery(id+"F0.wireOp",EDGE,"E0.right"),sQuery(id+"F0.wireOp",EDGE,"E1.bottom"),sQuery(id+"F0.wireOp",EDGE,"E1.top"),sQuery(id+"F0.wireOp",EDGE,"E1.left"),subQ0,sQuery(id+"F0.wireOp",EDGE,"E2"),sQuery(id+"F0.wireOp",EDGE,"VLRDwp0t-7qAt-eu2T-jZEU-YPBGhESBlTfT"),sQuery(id+"F0.wireOp",EDGE,"WEYKgsFz-RtNv-legM-eSOE-KK9nOp16vvV1"),sQuery(id+"F0.wireOp",EDGE,"XJheyNme-LiQL-8ZLm-PUsm-MQK8YgGBS3Id")])],"isStart":true})]});}
            var Q11;
            {var subQ0=sQuery(id+"F0.wireOp",EDGE,"E1.top");Q11=makeQuery(id+"F2.opChamfer","BLEND_EDGE",EDGE,{"blendedFrom":[makeQuery(id+"F1.opExtrude","CAP_EDGE",EDGE,{"disambiguationData":[OSD([subQ0])],"isStart":true}),makeQuery(id+"F1.opExtrude","CAP_FACE",FACE,{"disambiguationData":[OSD([sQuery(id+"F0.wireOp",EDGE,"E0.bottom"),sQuery(id+"F0.wireOp",EDGE,"E0.top"),sQuery(id+"F0.wireOp",EDGE,"E0.left"),sQuery(id+"F0.wireOp",EDGE,"E0.right"),sQuery(id+"F0.wireOp",EDGE,"E1.bottom"),subQ0,sQuery(id+"F0.wireOp",EDGE,"E1.left"),sQuery(id+"F0.wireOp",EDGE,"E1.right"),sQuery(id+"F0.wireOp",EDGE,"E2"),sQuery(id+"F0.wireOp",EDGE,"VLRDwp0t-7qAt-eu2T-jZEU-YPBGhESBlTfT"),sQuery(id+"F0.wireOp",EDGE,"WEYKgsFz-RtNv-legM-eSOE-KK9nOp16vvV1"),sQuery(id+"F0.wireOp",EDGE,"XJheyNme-LiQL-8ZLm-PUsm-MQK8YgGBS3Id")])],"isStart":true})],"blendedInto":[makeQuery(id+"F1.opExtrude","CAP_FACE",FACE,{"disambiguationData":[OSD([sQuery(id+"F0.wireOp",EDGE,"E0.bottom"),sQuery(id+"F0.wireOp",EDGE,"E0.top"),sQuery(id+"F0.wireOp",EDGE,"E0.left"),sQuery(id+"F0.wireOp",EDGE,"E0.right"),sQuery(id+"F0.wireOp",EDGE,"E1.bottom"),subQ0,sQuery(id+"F0.wireOp",EDGE,"E1.left"),sQuery(id+"F0.wireOp",EDGE,"E1.right"),sQuery(id+"F0.wireOp",EDGE,"E2"),sQuery(id+"F0.wireOp",EDGE,"VLRDwp0t-7qAt-eu2T-jZEU-YPBGhESBlTfT"),sQuery(id+"F0.wireOp",EDGE,"WEYKgsFz-RtNv-legM-eSOE-KK9nOp16vvV1"),sQuery(id+"F0.wireOp",EDGE,"XJheyNme-LiQL-8ZLm-PUsm-MQK8YgGBS3Id")])],"isStart":true})]});}
            var Q12;
            {var subQ0=sQuery(id+"F0.wireOp",EDGE,"E1.left");Q12=makeQuery(id+"F2.opChamfer","BLEND_EDGE",EDGE,{"blendedFrom":[makeQuery(id+"F1.opExtrude","CAP_EDGE",EDGE,{"disambiguationData":[OSD([subQ0])],"isStart":true}),makeQuery(id+"F1.opExtrude","CAP_FACE",FACE,{"disambiguationData":[OSD([sQuery(id+"F0.wireOp",EDGE,"E0.bottom"),sQuery(id+"F0.wireOp",EDGE,"E0.top"),sQuery(id+"F0.wireOp",EDGE,"E0.left"),sQuery(id+"F0.wireOp",EDGE,"E0.right"),sQuery(id+"F0.wireOp",EDGE,"E1.bottom"),sQuery(id+"F0.wireOp",EDGE,"E1.top"),subQ0,sQuery(id+"F0.wireOp",EDGE,"E1.right"),sQuery(id+"F0.wireOp",EDGE,"E2"),sQuery(id+"F0.wireOp",EDGE,"VLRDwp0t-7qAt-eu2T-jZEU-YPBGhESBlTfT"),sQuery(id+"F0.wireOp",EDGE,"WEYKgsFz-RtNv-legM-eSOE-KK9nOp16vvV1"),sQuery(id+"F0.wireOp",EDGE,"XJheyNme-LiQL-8ZLm-PUsm-MQK8YgGBS3Id")])],"isStart":true})],"blendedInto":[makeQuery(id+"F1.opExtrude","CAP_FACE",FACE,{"disambiguationData":[OSD([sQuery(id+"F0.wireOp",EDGE,"E0.bottom"),sQuery(id+"F0.wireOp",EDGE,"E0.top"),sQuery(id+"F0.wireOp",EDGE,"E0.left"),sQuery(id+"F0.wireOp",EDGE,"E0.right"),sQuery(id+"F0.wireOp",EDGE,"E1.bottom"),sQuery(id+"F0.wireOp",EDGE,"E1.top"),subQ0,sQuery(id+"F0.wireOp",EDGE,"E1.right"),sQuery(id+"F0.wireOp",EDGE,"E2"),sQuery(id+"F0.wireOp",EDGE,"VLRDwp0t-7qAt-eu2T-jZEU-YPBGhESBlTfT"),sQuery(id+"F0.wireOp",EDGE,"WEYKgsFz-RtNv-legM-eSOE-KK9nOp16vvV1"),sQuery(id+"F0.wireOp",EDGE,"XJheyNme-LiQL-8ZLm-PUsm-MQK8YgGBS3Id")])],"isStart":true})]});}
            var Q13;
            {var subQ0=sQuery(id+"F0.wireOp",EDGE,"E2");var subQ1=sQuery(id+"F0.wireOp",EDGE,"E1.left");var subQ2=sQuery(id+"F0.wireOp",EDGE,"E0.bottom");Q13=makeQuery(id+"F2.opChamfer","BLEND_EDGE",EDGE,{"blendedFrom":[makeQuery(id+"F1.opExtrude","CAP_EDGE",EDGE,{"disambiguationData":[OSD([subQ0]),TDD([makeQuery(id+"F0.imprint","IMPRINT",EDGE,{"disambiguationData":[TD([[makeQuery(id+"F0.imprint","INTERSECT",VERTEX,{"derivedFrom":[subQ2,subQ0]}),-1.0]])],"derivedFrom":subQ0})])],"isStart":true}),makeQuery(id+"F1.opExtrude","CAP_FACE",FACE,{"disambiguationData":[OSD([subQ2,sQuery(id+"F0.wireOp",EDGE,"E0.top"),sQuery(id+"F0.wireOp",EDGE,"E0.left"),sQuery(id+"F0.wireOp",EDGE,"E0.right"),sQuery(id+"F0.wireOp",EDGE,"E1.bottom"),sQuery(id+"F0.wireOp",EDGE,"E1.top"),subQ1,sQuery(id+"F0.wireOp",EDGE,"E1.right"),subQ0,sQuery(id+"F0.wireOp",EDGE,"VLRDwp0t-7qAt-eu2T-jZEU-YPBGhESBlTfT"),sQuery(id+"F0.wireOp",EDGE,"WEYKgsFz-RtNv-legM-eSOE-KK9nOp16vvV1"),sQuery(id+"F0.wireOp",EDGE,"XJheyNme-LiQL-8ZLm-PUsm-MQK8YgGBS3Id")])],"isStart":true})],"blendedInto":[makeQuery(id+"F1.opExtrude","CAP_FACE",FACE,{"disambiguationData":[OSD([subQ2,sQuery(id+"F0.wireOp",EDGE,"E0.top"),sQuery(id+"F0.wireOp",EDGE,"E0.left"),sQuery(id+"F0.wireOp",EDGE,"E0.right"),sQuery(id+"F0.wireOp",EDGE,"E1.bottom"),sQuery(id+"F0.wireOp",EDGE,"E1.top"),subQ1,sQuery(id+"F0.wireOp",EDGE,"E1.right"),subQ0,sQuery(id+"F0.wireOp",EDGE,"VLRDwp0t-7qAt-eu2T-jZEU-YPBGhESBlTfT"),sQuery(id+"F0.wireOp",EDGE,"WEYKgsFz-RtNv-legM-eSOE-KK9nOp16vvV1"),sQuery(id+"F0.wireOp",EDGE,"XJheyNme-LiQL-8ZLm-PUsm-MQK8YgGBS3Id")])],"isStart":true})]});}
            var Q14;
            {var subQ0=sQuery(id+"F0.wireOp",EDGE,"E0.bottom");Q14=makeQuery(id+"F2.opChamfer","BLEND_EDGE",EDGE,{"blendedFrom":[makeQuery(id+"F1.opExtrude","CAP_EDGE",EDGE,{"disambiguationData":[OSD([subQ0])],"isStart":true}),makeQuery(id+"F1.opExtrude","CAP_FACE",FACE,{"disambiguationData":[OSD([subQ0,sQuery(id+"F0.wireOp",EDGE,"E0.top"),sQuery(id+"F0.wireOp",EDGE,"E0.left"),sQuery(id+"F0.wireOp",EDGE,"E0.right"),sQuery(id+"F0.wireOp",EDGE,"E1.bottom"),sQuery(id+"F0.wireOp",EDGE,"E1.top"),sQuery(id+"F0.wireOp",EDGE,"E1.left"),sQuery(id+"F0.wireOp",EDGE,"E1.right"),sQuery(id+"F0.wireOp",EDGE,"E2"),sQuery(id+"F0.wireOp",EDGE,"VLRDwp0t-7qAt-eu2T-jZEU-YPBGhESBlTfT"),sQuery(id+"F0.wireOp",EDGE,"WEYKgsFz-RtNv-legM-eSOE-KK9nOp16vvV1"),sQuery(id+"F0.wireOp",EDGE,"XJheyNme-LiQL-8ZLm-PUsm-MQK8YgGBS3Id")])],"isStart":true})],"blendedInto":[makeQuery(id+"F1.opExtrude","CAP_FACE",FACE,{"disambiguationData":[OSD([subQ0,sQuery(id+"F0.wireOp",EDGE,"E0.top"),sQuery(id+"F0.wireOp",EDGE,"E0.left"),sQuery(id+"F0.wireOp",EDGE,"E0.right"),sQuery(id+"F0.wireOp",EDGE,"E1.bottom"),sQuery(id+"F0.wireOp",EDGE,"E1.top"),sQuery(id+"F0.wireOp",EDGE,"E1.left"),sQuery(id+"F0.wireOp",EDGE,"E1.right"),sQuery(id+"F0.wireOp",EDGE,"E2"),sQuery(id+"F0.wireOp",EDGE,"VLRDwp0t-7qAt-eu2T-jZEU-YPBGhESBlTfT"),sQuery(id+"F0.wireOp",EDGE,"WEYKgsFz-RtNv-legM-eSOE-KK9nOp16vvV1"),sQuery(id+"F0.wireOp",EDGE,"XJheyNme-LiQL-8ZLm-PUsm-MQK8YgGBS3Id")])],"isStart":true})]});}
            var Q15;
            {var subQ0=sQuery(id+"F0.wireOp",EDGE,"E0.right");Q15=makeQuery(id+"F2.opChamfer","BLEND_EDGE",EDGE,{"blendedFrom":[makeQuery(id+"F1.opExtrude","CAP_EDGE",EDGE,{"disambiguationData":[OSD([subQ0])],"isStart":true}),makeQuery(id+"F1.opExtrude","CAP_FACE",FACE,{"disambiguationData":[OSD([sQuery(id+"F0.wireOp",EDGE,"E0.bottom"),sQuery(id+"F0.wireOp",EDGE,"E0.top"),sQuery(id+"F0.wireOp",EDGE,"E0.left"),subQ0,sQuery(id+"F0.wireOp",EDGE,"E1.bottom"),sQuery(id+"F0.wireOp",EDGE,"E1.top"),sQuery(id+"F0.wireOp",EDGE,"E1.left"),sQuery(id+"F0.wireOp",EDGE,"E1.right"),sQuery(id+"F0.wireOp",EDGE,"E2"),sQuery(id+"F0.wireOp",EDGE,"VLRDwp0t-7qAt-eu2T-jZEU-YPBGhESBlTfT"),sQuery(id+"F0.wireOp",EDGE,"WEYKgsFz-RtNv-legM-eSOE-KK9nOp16vvV1"),sQuery(id+"F0.wireOp",EDGE,"XJheyNme-LiQL-8ZLm-PUsm-MQK8YgGBS3Id")])],"isStart":true})],"blendedInto":[makeQuery(id+"F1.opExtrude","CAP_FACE",FACE,{"disambiguationData":[OSD([sQuery(id+"F0.wireOp",EDGE,"E0.bottom"),sQuery(id+"F0.wireOp",EDGE,"E0.top"),sQuery(id+"F0.wireOp",EDGE,"E0.left"),subQ0,sQuery(id+"F0.wireOp",EDGE,"E1.bottom"),sQuery(id+"F0.wireOp",EDGE,"E1.top"),sQuery(id+"F0.wireOp",EDGE,"E1.left"),sQuery(id+"F0.wireOp",EDGE,"E1.right"),sQuery(id+"F0.wireOp",EDGE,"E2"),sQuery(id+"F0.wireOp",EDGE,"VLRDwp0t-7qAt-eu2T-jZEU-YPBGhESBlTfT"),sQuery(id+"F0.wireOp",EDGE,"WEYKgsFz-RtNv-legM-eSOE-KK9nOp16vvV1"),sQuery(id+"F0.wireOp",EDGE,"XJheyNme-LiQL-8ZLm-PUsm-MQK8YgGBS3Id")])],"isStart":true})]});}
            var Q16;
            {var subQ0=sQuery(id+"F0.wireOp",EDGE,"E0.top");Q16=makeQuery(id+"F2.opChamfer","BLEND_EDGE",EDGE,{"blendedFrom":[makeQuery(id+"F1.opExtrude","CAP_EDGE",EDGE,{"disambiguationData":[OSD([subQ0])],"isStart":true}),makeQuery(id+"F1.opExtrude","CAP_FACE",FACE,{"disambiguationData":[OSD([sQuery(id+"F0.wireOp",EDGE,"E0.bottom"),subQ0,sQuery(id+"F0.wireOp",EDGE,"E0.left"),sQuery(id+"F0.wireOp",EDGE,"E0.right"),sQuery(id+"F0.wireOp",EDGE,"E1.bottom"),sQuery(id+"F0.wireOp",EDGE,"E1.top"),sQuery(id+"F0.wireOp",EDGE,"E1.left"),sQuery(id+"F0.wireOp",EDGE,"E1.right"),sQuery(id+"F0.wireOp",EDGE,"E2"),sQuery(id+"F0.wireOp",EDGE,"VLRDwp0t-7qAt-eu2T-jZEU-YPBGhESBlTfT"),sQuery(id+"F0.wireOp",EDGE,"WEYKgsFz-RtNv-legM-eSOE-KK9nOp16vvV1"),sQuery(id+"F0.wireOp",EDGE,"XJheyNme-LiQL-8ZLm-PUsm-MQK8YgGBS3Id")])],"isStart":true})],"blendedInto":[makeQuery(id+"F1.opExtrude","CAP_FACE",FACE,{"disambiguationData":[OSD([sQuery(id+"F0.wireOp",EDGE,"E0.bottom"),subQ0,sQuery(id+"F0.wireOp",EDGE,"E0.left"),sQuery(id+"F0.wireOp",EDGE,"E0.right"),sQuery(id+"F0.wireOp",EDGE,"E1.bottom"),sQuery(id+"F0.wireOp",EDGE,"E1.top"),sQuery(id+"F0.wireOp",EDGE,"E1.left"),sQuery(id+"F0.wireOp",EDGE,"E1.right"),sQuery(id+"F0.wireOp",EDGE,"E2"),sQuery(id+"F0.wireOp",EDGE,"VLRDwp0t-7qAt-eu2T-jZEU-YPBGhESBlTfT"),sQuery(id+"F0.wireOp",EDGE,"WEYKgsFz-RtNv-legM-eSOE-KK9nOp16vvV1"),sQuery(id+"F0.wireOp",EDGE,"XJheyNme-LiQL-8ZLm-PUsm-MQK8YgGBS3Id")])],"isStart":true})]});}
            var Q17;
            {var subQ0=sQuery(id+"F0.wireOp",EDGE,"E0.left");Q17=makeQuery(id+"F2.opChamfer","BLEND_EDGE",EDGE,{"blendedFrom":[makeQuery(id+"F1.opExtrude","CAP_EDGE",EDGE,{"disambiguationData":[OSD([subQ0])],"isStart":true}),makeQuery(id+"F1.opExtrude","CAP_FACE",FACE,{"disambiguationData":[OSD([sQuery(id+"F0.wireOp",EDGE,"E0.bottom"),sQuery(id+"F0.wireOp",EDGE,"E0.top"),subQ0,sQuery(id+"F0.wireOp",EDGE,"E0.right"),sQuery(id+"F0.wireOp",EDGE,"E1.bottom"),sQuery(id+"F0.wireOp",EDGE,"E1.top"),sQuery(id+"F0.wireOp",EDGE,"E1.left"),sQuery(id+"F0.wireOp",EDGE,"E1.right"),sQuery(id+"F0.wireOp",EDGE,"E2"),sQuery(id+"F0.wireOp",EDGE,"VLRDwp0t-7qAt-eu2T-jZEU-YPBGhESBlTfT"),sQuery(id+"F0.wireOp",EDGE,"WEYKgsFz-RtNv-legM-eSOE-KK9nOp16vvV1"),sQuery(id+"F0.wireOp",EDGE,"XJheyNme-LiQL-8ZLm-PUsm-MQK8YgGBS3Id")])],"isStart":true})],"blendedInto":[makeQuery(id+"F1.opExtrude","CAP_FACE",FACE,{"disambiguationData":[OSD([sQuery(id+"F0.wireOp",EDGE,"E0.bottom"),sQuery(id+"F0.wireOp",EDGE,"E0.top"),subQ0,sQuery(id+"F0.wireOp",EDGE,"E0.right"),sQuery(id+"F0.wireOp",EDGE,"E1.bottom"),sQuery(id+"F0.wireOp",EDGE,"E1.top"),sQuery(id+"F0.wireOp",EDGE,"E1.left"),sQuery(id+"F0.wireOp",EDGE,"E1.right"),sQuery(id+"F0.wireOp",EDGE,"E2"),sQuery(id+"F0.wireOp",EDGE,"VLRDwp0t-7qAt-eu2T-jZEU-YPBGhESBlTfT"),sQuery(id+"F0.wireOp",EDGE,"WEYKgsFz-RtNv-legM-eSOE-KK9nOp16vvV1"),sQuery(id+"F0.wireOp",EDGE,"XJheyNme-LiQL-8ZLm-PUsm-MQK8YgGBS3Id")])],"isStart":true})]});}
            var Q18;
            {var subQ0=sQuery(id+"F0.wireOp",EDGE,"E2");var subQ1=sQuery(id+"F0.wireOp",EDGE,"E1.bottom");var subQ2=sQuery(id+"F0.wireOp",EDGE,"E0.left");Q18=makeQuery(id+"F2.opChamfer","BLEND_EDGE",EDGE,{"blendedFrom":[makeQuery(id+"F1.opExtrude","CAP_EDGE",EDGE,{"disambiguationData":[OSD([subQ0]),TDD([makeQuery(id+"F0.imprint","IMPRINT",EDGE,{"disambiguationData":[TD([[makeQuery(id+"F0.imprint","INTERSECT",VERTEX,{"derivedFrom":[subQ2,subQ0]}),1.0]])],"derivedFrom":subQ0})])],"isStart":true}),makeQuery(id+"F1.opExtrude","CAP_FACE",FACE,{"disambiguationData":[OSD([sQuery(id+"F0.wireOp",EDGE,"E0.bottom"),sQuery(id+"F0.wireOp",EDGE,"E0.top"),subQ2,sQuery(id+"F0.wireOp",EDGE,"E0.right"),subQ1,sQuery(id+"F0.wireOp",EDGE,"E1.top"),sQuery(id+"F0.wireOp",EDGE,"E1.left"),sQuery(id+"F0.wireOp",EDGE,"E1.right"),subQ0,sQuery(id+"F0.wireOp",EDGE,"VLRDwp0t-7qAt-eu2T-jZEU-YPBGhESBlTfT"),sQuery(id+"F0.wireOp",EDGE,"WEYKgsFz-RtNv-legM-eSOE-KK9nOp16vvV1"),sQuery(id+"F0.wireOp",EDGE,"XJheyNme-LiQL-8ZLm-PUsm-MQK8YgGBS3Id")])],"isStart":true})],"blendedInto":[makeQuery(id+"F1.opExtrude","CAP_FACE",FACE,{"disambiguationData":[OSD([sQuery(id+"F0.wireOp",EDGE,"E0.bottom"),sQuery(id+"F0.wireOp",EDGE,"E0.top"),subQ2,sQuery(id+"F0.wireOp",EDGE,"E0.right"),subQ1,sQuery(id+"F0.wireOp",EDGE,"E1.top"),sQuery(id+"F0.wireOp",EDGE,"E1.left"),sQuery(id+"F0.wireOp",EDGE,"E1.right"),subQ0,sQuery(id+"F0.wireOp",EDGE,"VLRDwp0t-7qAt-eu2T-jZEU-YPBGhESBlTfT"),sQuery(id+"F0.wireOp",EDGE,"WEYKgsFz-RtNv-legM-eSOE-KK9nOp16vvV1"),sQuery(id+"F0.wireOp",EDGE,"XJheyNme-LiQL-8ZLm-PUsm-MQK8YgGBS3Id")])],"isStart":true})]});}
            var Q19;
            {var subQ0=sQuery(id+"F0.wireOp",EDGE,"E1.bottom");Q19=makeQuery(id+"F2.opChamfer","BLEND_EDGE",EDGE,{"blendedFrom":[makeQuery(id+"F1.opExtrude","CAP_EDGE",EDGE,{"disambiguationData":[OSD([subQ0])],"isStart":true}),makeQuery(id+"F1.opExtrude","CAP_FACE",FACE,{"disambiguationData":[OSD([sQuery(id+"F0.wireOp",EDGE,"E0.bottom"),sQuery(id+"F0.wireOp",EDGE,"E0.top"),sQuery(id+"F0.wireOp",EDGE,"E0.left"),sQuery(id+"F0.wireOp",EDGE,"E0.right"),subQ0,sQuery(id+"F0.wireOp",EDGE,"E1.top"),sQuery(id+"F0.wireOp",EDGE,"E1.left"),sQuery(id+"F0.wireOp",EDGE,"E1.right"),sQuery(id+"F0.wireOp",EDGE,"E2"),sQuery(id+"F0.wireOp",EDGE,"VLRDwp0t-7qAt-eu2T-jZEU-YPBGhESBlTfT"),sQuery(id+"F0.wireOp",EDGE,"WEYKgsFz-RtNv-legM-eSOE-KK9nOp16vvV1"),sQuery(id+"F0.wireOp",EDGE,"XJheyNme-LiQL-8ZLm-PUsm-MQK8YgGBS3Id")])],"isStart":true})],"blendedInto":[makeQuery(id+"F1.opExtrude","CAP_FACE",FACE,{"disambiguationData":[OSD([sQuery(id+"F0.wireOp",EDGE,"E0.bottom"),sQuery(id+"F0.wireOp",EDGE,"E0.top"),sQuery(id+"F0.wireOp",EDGE,"E0.left"),sQuery(id+"F0.wireOp",EDGE,"E0.right"),subQ0,sQuery(id+"F0.wireOp",EDGE,"E1.top"),sQuery(id+"F0.wireOp",EDGE,"E1.left"),sQuery(id+"F0.wireOp",EDGE,"E1.right"),sQuery(id+"F0.wireOp",EDGE,"E2"),sQuery(id+"F0.wireOp",EDGE,"VLRDwp0t-7qAt-eu2T-jZEU-YPBGhESBlTfT"),sQuery(id+"F0.wireOp",EDGE,"WEYKgsFz-RtNv-legM-eSOE-KK9nOp16vvV1"),sQuery(id+"F0.wireOp",EDGE,"XJheyNme-LiQL-8ZLm-PUsm-MQK8YgGBS3Id")])],"isStart":true})]});}
            chamfer(context, id + "F3", {"entities" : qUnion([Q0, Q1, Q2, Q3, Q4, Q5, Q6, Q7, Q8, Q9, Q10, Q11, Q12, Q13, Q14, Q15, Q16, Q17, Q18, Q19]), "width" : 0.5 * mm, "tangentPropagation" : true});
        }
        {
            var Q0;
            Q0=makeQuery(id+"F1.opExtrude","CAP_FACE",FACE,{"disambiguationData":[OSD([sQuery(id+"F0.wireOp",EDGE,"E0.bottom"),sQuery(id+"F0.wireOp",EDGE,"E0.top"),sQuery(id+"F0.wireOp",EDGE,"E0.left"),sQuery(id+"F0.wireOp",EDGE,"E0.right"),sQuery(id+"F0.wireOp",EDGE,"E1.bottom"),sQuery(id+"F0.wireOp",EDGE,"E1.top"),sQuery(id+"F0.wireOp",EDGE,"E1.left"),sQuery(id+"F0.wireOp",EDGE,"E1.right"),sQuery(id+"F0.wireOp",EDGE,"E2"),sQuery(id+"F0.wireOp",EDGE,"E3"),sQuery(id+"F0.wireOp",EDGE,"E4"),sQuery(id+"F0.wireOp",EDGE,"E5")])],"isStart":false});
            var sketch = newSketch(context, id + "F4", { "sketchPlane" : qUnion([Q0])});
            skLineSegment(sketch, "E10.bottom", {"start": v(-33.03, 33.03) * mm, "end": v(-3.06, 33.03) * mm});
            skLineSegment(sketch, "E10.top", {"start": v(-33.03, 3) * mm, "end": v(-3.06, 3) * mm});
            skLineSegment(sketch, "E10.left", {"start": v(-33.03, 33.03) * mm, "end": v(-33.03, 3) * mm});
            skLineSegment(sketch, "E10.right", {"start": v(-3.06, 33.03) * mm, "end": v(-3.06, 3) * mm});
            skLineSegment(sketch, "E11.bottom", {"start": v(3.05, -33.03) * mm, "end": v(33.03, -33.03) * mm});
            skLineSegment(sketch, "E11.top", {"start": v(3.05, -3.05) * mm, "end": v(33.03, -3.05) * mm});
            skLineSegment(sketch, "E11.left", {"start": v(3.05, -33.03) * mm, "end": v(3.05, -3.05) * mm});
            skLineSegment(sketch, "E11.right", {"start": v(33.03, -33.03) * mm, "end": v(33.03, -3.05) * mm});
            skLineSegment(sketch, "E12.bottom", {"start": v(36.1, -36.12) * mm, "end": v(-36.17, -36.12) * mm});
            skLineSegment(sketch, "E12.top", {"start": v(36.1, 36.08) * mm, "end": v(-36.17, 36.08) * mm});
            skLineSegment(sketch, "E12.left", {"start": v(36.1, -36.12) * mm, "end": v(36.1, 36.08) * mm});
            skLineSegment(sketch, "E12.right", {"start": v(-36.17, -36.12) * mm, "end": v(-36.17, 36.08) * mm});
            skLineSegment(sketch, "E13.bottom", {"start": v(-36.17, 3.05) * mm, "end": v(-19.12, 3.05) * mm});
            skLineSegment(sketch, "E13.top", {"start": v(-36.17, -45.58) * mm, "end": v(-19.12, -45.58) * mm});
            skLineSegment(sketch, "E13.left", {"start": v(-36.17, 3.05) * mm, "end": v(-36.17, -45.58) * mm});
            skLineSegment(sketch, "E13.right", {"start": v(-19.12, 3.05) * mm, "end": v(-19.12, -45.58) * mm});
            skLineSegment(sketch, "E14.bottom", {"start": v(3.05, -36.12) * mm, "end": v(-15.8, -36.12) * mm});
            skLineSegment(sketch, "E14.top", {"start": v(3.05, -19.5) * mm, "end": v(-15.8, -19.5) * mm});
            skLineSegment(sketch, "E14.left", {"start": v(3.05, -36.12) * mm, "end": v(3.05, -19.5) * mm});
            skLineSegment(sketch, "E14.right", {"start": v(-15.8, -36.12) * mm, "end": v(-15.8, -19.5) * mm});
            skLineSegment(sketch, "E15.bottom", {"start": v(-3.05, 36.08) * mm, "end": v(25.52, 36.08) * mm});
            skLineSegment(sketch, "E15.top", {"start": v(-3.05, 19.17) * mm, "end": v(25.52, 19.17) * mm});
            skLineSegment(sketch, "E15.left", {"start": v(-3.05, 36.08) * mm, "end": v(-3.05, 19.17) * mm});
            skLineSegment(sketch, "E15.right", {"start": v(25.52, 36.08) * mm, "end": v(25.52, 19.17) * mm});
            skLineSegment(sketch, "E16.bottom", {"start": v(36.1, -3.05) * mm, "end": v(19.54, -3.05) * mm});
            skLineSegment(sketch, "E16.top", {"start": v(36.1, 5.67) * mm, "end": v(19.54, 5.67) * mm});
            skLineSegment(sketch, "E16.left", {"start": v(36.1, -3.05) * mm, "end": v(36.1, 5.67) * mm});
            skLineSegment(sketch, "E16.right", {"start": v(19.54, -3.05) * mm, "end": v(19.54, 5.67) * mm});
            skCircle(sketch, "E17", {"center": v(-36.17, 36.08) * mm, "radius": 8 * mm});
            skCircle(sketch, "E18", {"center": v(36.1, -36.12) * mm, "radius": 8 * mm});
            skSolve(sketch);
        }
        {
            var Q0;
            {var subQ0=sQuery(id+"F4.wireOp",EDGE,"E12.right");var subQ1=sQuery(id+"F4.wireOp",EDGE,"E12.top");var subQ2=makeQuery(id+"F4.imprint","INTERSECT",VERTEX,{"derivedFrom":[subQ1,subQ0]});Q0=makeQuery(id+"F4.imprint","IMPRINT",FACE,{"disambiguationData":[TD([[makeQuery(id+"F4.imprint","IMPRINT",EDGE,{"disambiguationData":[TD([[subQ2,1.0]])],"derivedFrom":subQ1}),-1.0]])]});}
            var Q1;
            {var subQ6=sQuery(id+"F4.wireOp",EDGE,"E10.left");var subQ7=sQuery(id+"F4.wireOp",EDGE,"E10.bottom");var subQ8=makeQuery(id+"F4.imprint","INTERSECT",VERTEX,{"derivedFrom":[subQ7,subQ6]});Q1=makeQuery(id+"F4.imprint","IMPRINT",FACE,{"disambiguationData":[TD([[makeQuery(id+"F4.imprint","IMPRINT",EDGE,{"disambiguationData":[TD([[subQ8,1.0]])],"derivedFrom":subQ7}),-1.0]])]});}
            var Q2;
            {var subQ0=sQuery(id+"F4.wireOp",EDGE,"E10.left");var subQ1=sQuery(id+"F4.wireOp",EDGE,"E10.bottom");var subQ2=makeQuery(id+"F4.imprint","INTERSECT",VERTEX,{"derivedFrom":[subQ1,subQ0]});Q2=makeQuery(id+"F4.imprint","IMPRINT",FACE,{"disambiguationData":[TD([[makeQuery(id+"F4.imprint","IMPRINT",EDGE,{"disambiguationData":[TD([[subQ2,1.0]])],"derivedFrom":subQ1}),1.0]])]});}
            var Q3;
            {var subQ6=sQuery(id+"F4.wireOp",EDGE,"E11.right");var subQ7=sQuery(id+"F4.wireOp",EDGE,"E11.bottom");var subQ8=makeQuery(id+"F4.imprint","INTERSECT",VERTEX,{"derivedFrom":[subQ7,subQ6]});Q3=makeQuery(id+"F4.imprint","IMPRINT",FACE,{"disambiguationData":[TD([[makeQuery(id+"F4.imprint","IMPRINT",EDGE,{"disambiguationData":[TD([[subQ8,1.0]])],"derivedFrom":subQ7}),-1.0]])]});}
            var Q4;
            {var subQ0=sQuery(id+"F4.wireOp",EDGE,"E12.left");var subQ1=sQuery(id+"F4.wireOp",EDGE,"E12.bottom");var subQ2=makeQuery(id+"F4.imprint","INTERSECT",VERTEX,{"derivedFrom":[subQ1,subQ0]});Q4=makeQuery(id+"F4.imprint","IMPRINT",FACE,{"disambiguationData":[TD([[makeQuery(id+"F4.imprint","IMPRINT",EDGE,{"disambiguationData":[TD([[subQ2,-1.0]])],"derivedFrom":subQ1}),1.0]])]});}
            var Q5;
            {var subQ0=sQuery(id+"F4.wireOp",EDGE,"E11.right");var subQ1=sQuery(id+"F4.wireOp",EDGE,"E11.bottom");var subQ2=makeQuery(id+"F4.imprint","INTERSECT",VERTEX,{"derivedFrom":[subQ1,subQ0]});Q5=makeQuery(id+"F4.imprint","IMPRINT",FACE,{"disambiguationData":[TD([[makeQuery(id+"F4.imprint","IMPRINT",EDGE,{"disambiguationData":[TD([[subQ2,1.0]])],"derivedFrom":subQ1}),1.0]])]});}
            extrude(context, id + "F5", {"entities" : qUnion([Q0, Q1, Q2, Q3, Q4, Q5]), "operationType" : NewBodyOperationType.REMOVE, "surfaceOperationType" : NewSurfaceOperationType.ADD, "endBound" : BoundingType.THROUGH_ALL, "oppositeDirection" : true, "depth" : 25 * mm, "offsetDistance" : 25 * mm});
        }
    });
